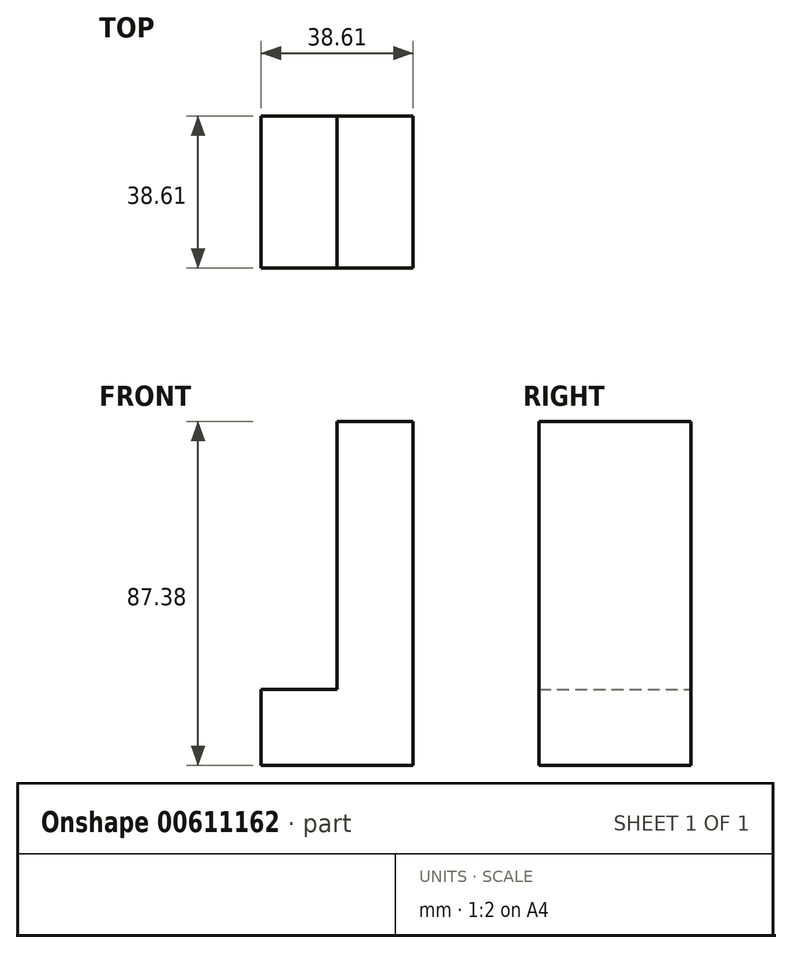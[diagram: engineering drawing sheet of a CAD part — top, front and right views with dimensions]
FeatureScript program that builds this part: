
annotation { "Feature Type Name" : "Feature", "Feature Type Description" : "" }
export const myFeature = defineFeature(function(context is Context, id is Id, definition is map)
    precondition{}
    {
        {
            var Q0;
            Q0=qCreatedBy(makeId("Front.planeOp"),FACE);
            var sketch = newSketch(context, id + "F0", { "sketchPlane" : qUnion([Q0])});
            skLineSegment(sketch, "E0", {"start": v(0, 0) * mm, "end": v(0, 19.3) * mm});
            skLineSegment(sketch, "E1", {"start": v(0, 19.3) * mm, "end": v(19.3, 19.3) * mm});
            skLineSegment(sketch, "E2", {"start": v(19.3, 19.3) * mm, "end": v(19.3, 87.38) * mm});
            skLineSegment(sketch, "E3", {"start": v(19.3, 87.38) * mm, "end": v(38.6, 87.38) * mm});
            skLineSegment(sketch, "E4", {"start": v(38.6, 87.38) * mm, "end": v(38.6, 0) * mm});
            skLineSegment(sketch, "E5", {"start": v(38.6, 0) * mm, "end": v(0, 0) * mm});
            skSolve(sketch);
        }
        {
            var Q0;
            Q0=makeQuery(id+"F0.imprint","IMPRINT",FACE,{"disambiguationData":[TD([[makeQuery(id+"F0.imprint","IMPRINT",EDGE,{"derivedFrom":sQuery(id+"F0.wireOp",EDGE,"E0")}),-1.0]])]});
            extrude(context, id + "F1", {"entities" : qUnion([Q0]), "depth" : 38.6 * mm, "offsetDistance" : 25.4 * mm});
        }
    });
